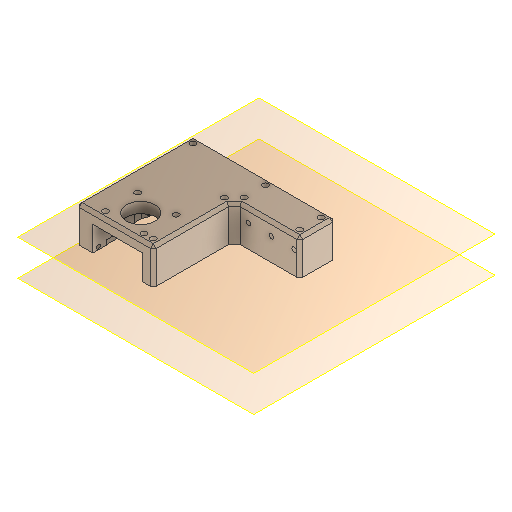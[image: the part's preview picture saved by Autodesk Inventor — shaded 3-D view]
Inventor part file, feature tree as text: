
AUTODESK INVENTOR PART (.ipt)
format: ipt  version: 2024.1 (Build 281209000, 209)  size: 345,088 bytes
history: native  units: mm
features: sketch x7, reference x7, other x6, projected_geometry x5, extrude x3, hole x3, plane x2, revolve x1, chamfer x1
ambient origin geometry x8: Origin, YZ Plane, XZ Plane, XY Plane, X Axis, Y Axis, Z Axis, Center Point
bodies: Volumenkörper1 (feature_tree)
feature tree (35):
  plane  "Arbeitsebene2"
  extrude  "Extrusion1"  TaperAngle=135.0deg  [1 undecoded]
  revolve  "Umdrehung1"
  chamfer  "Fasen1"  Distance=10.0mm
  hole  "Bohrung1"  [1 undecoded]
  extrude  "Extrusion2"  Depth=2.0mm TaperAngle=45.0deg
  hole  "Bohrung2"  [1 undecoded]
  hole  "Bohrung3"  [1 undecoded]
  extrude  "Extrusion3"  Depth=22.5mm
  plane  "Arbeitsebene1"
  sketch  "Skizze1"  dims[d0=25.0mm d1=135.0deg]
  reference  "Referenz1"
  reference  "Referenz2"
  reference  "Referenz3"
  reference  "Referenz4"
  sketch  "Skizze2"  dims[d2=8.0mm]
  reference  "Referenz5"
  sketch  "Skizze3"  dims[d3=0.0mm]
  projected_geometry  "Projizierte Kontur1"
  projected_geometry  "Projizierte Kontur2"
  projected_geometry  "Projizierte Kontur3"
  sketch  "Skizze4"  dims[d4=4.0mm]
  sketch  "Skizze5"  dims[d5=4.0mm]
  reference  "Referenz6"
  sketch  "Skizze6"  dims[d6=0.0mm d7=10.0mm d8=0.0mm]
  projected_geometry  "Projizierte Kontur4"
  sketch  "Skizze7"  dims[d9=35.0mm d10=360.0deg d11=2.0mm d12=2.0mm d13=45.0deg d14=3.0mm d15=3.2mm d16=6.0mm d17=4.0mm d18=6.0mm d19=90.0deg d20=1.0mm d21=0.0mm d24=35.0mm d25=0.0mm d26=22.5mm d27=3.2mm d28=6.0mm d29=6.5mm d30=16.0mm d31=90.0deg d32=8.0mm d33=0.0mm d34=0.3mm d35=2.0mm d36=2.8mm d37=6.0mm d38=6.5mm d39=16.0mm d40=90.0deg d41=20.0mm d42=0.0mm d43=20.0mm d44=35.0mm d45=0.0mm]
  reference  "Referenz7"
  projected_geometry  "Projizierte Kontur5"
  other  "Assembly_MicroscopeInABox_v0.iam"
  other  "00_Berrybase_CCTVLens_50mm:1"
  other  "Assembly_XYZ_Stage_Micrometer_ontop_lightsheet:1"
  other  "00_XYZstage_micro_LT-4047-S1:1"
  other  "00_10x_Objective_ViewSolutions_bm05073332:1"
  other  "40_XYZstage_micrometer_motorized_nema8_samplemount_lightsheet_screwed:1"
note: 4 required parameter values undecoded (feature->parameter linkage not recoverable at this tier; creation-order binding heuristic only, values carry confidence <= 0.55)
